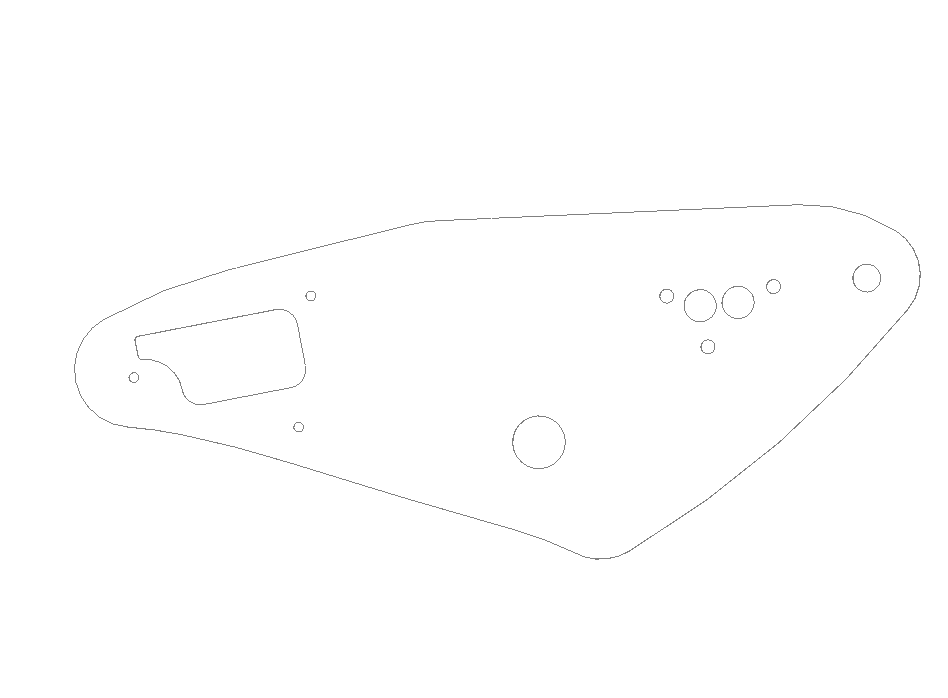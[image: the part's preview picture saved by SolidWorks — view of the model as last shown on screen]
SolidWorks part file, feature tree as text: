
SOLIDWORKS PART (.sldprt)
format: sldprt  version: not decoded by parser v0  size: 581,120 bytes
history: native  units: mm
features: sketch x7, cut_extrude x3, fillet x3, material x1, extrude x1 (+11 scaffold rows collapsed)
feature tree (26):
  scaffold x11  (default folders/planes/origin — collapsed)
  material  "Material <not specified>"
  sketch  "Sketch1"  dims[c1.D1=36.322mm c1.D14=19.177mm c1.D15=4.445mm c1.D16=~6.37032mm c1.D6=19.0754mm c1.D7=5.1054mm c1.D2=~199.24268mm c1.D3=~156.68752mm c1.D4=406.4mm c1.D5=50.8mm c2.D6=~27.88158mm c2.D7=5.4864mm c2.D8=~29.65196mm c2.D9=~99.15144mm c2.D10=~74.00036mm c2.D11=~83.60664mm c2.D12=43.5229mm c2.D13=~46.93158mm c2.D5=50.8mm c3.D6=22.225mm]
  sketch  "Sketch2"  dims[D7=9.652mm D1=~136.37006mm D2=~137.06094mm D3=~65.80124mm D4=~115.98402mm D5=~100.60432mm D6=~87.52586mm]
  sketch  "Sketch5"  dims[c1.D1=~25.32761mm c1.D2=69.85mm c1.D3=263.7258mm c1.D4=~100.720305mm c1.D6=~95.355191mm c1.D8=~731.379308mm c1.D9=~32.058621mm c1.D10=~96.585496mm c1.D7=~28.07208mm c2.D6=~28.30068mm c2.D9=~96.585496mm c2.D13=~32.058621mm c2.D14=203.2mm c2.D15=69.6087mm c2.D3=508.0mm c2.D4=~116.644653mm c2.D5=~98.588481mm c2.D1=~89.63152mm c3.D5=~247.693214mm c3.D7=~128.613829mm c3.D11=~89.631303mm c3.D12=~37.08194mm c4.D7=~128.613829mm c4.D10=~37.08194mm c4.D3=~247.693214mm c4.D5=~306.35078mm]
  sketch  "Sketch6"
  extrude  "Extrude1"  Depth=3.2512mm
  sketch  "Sketch7"  dims[c1.D15=6.7564mm c1.D1=6.35mm c1.D2=19.05mm c1.D3=16.2941mm c1.D4=86.36mm c1.D5=54.61mm c1.D6=~117.348901mm c1.D7=~31.878923mm c1.D8=~104.77653mm c1.D9=~54.921121mm c1.D10=~130.049857mm c1.D11=~67.888762mm c1.D12=~117.348901mm c2.D12=~26.580745deg c2.D13=~201.334457mm c2.D14=~33.122805mm c2.D16=~25.561602mm c3.D14=~25.56095mm c3.D2=25.4mm c3.D4=111.76mm c3.D5=54.61mm c3.D13=~117.696265mm]
  cut_extrude  "Cut-Extrude2"  [1 undecoded]
  fillet  "Fillet1"  Radius=2.54mm
  fillet  "Fillet2"  Radius=12.7mm
  fillet  "Fillet3"  Radius=25.4mm
  sketch  "Sketch8"  dims[D1=22.225mm]
  cut_extrude  "Cut-Extrude3"  [1 undecoded]
  sketch  "Sketch9"  dims[D1=1.5875mm]
  cut_extrude  "Cut-Extrude4"  [1 undecoded]
decode coverage: 10 of 14 modeling features carry decoded parameters
note: ~ marks probable driven/reference dimensions
note: 3 parameter values undecoded
summary: no parameter record found for 3 features
note: suppression state not decoded; provenance and decode notes live in map.json
